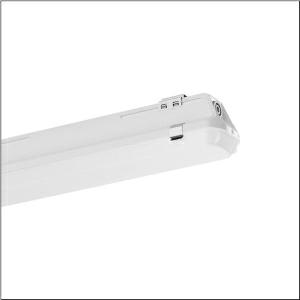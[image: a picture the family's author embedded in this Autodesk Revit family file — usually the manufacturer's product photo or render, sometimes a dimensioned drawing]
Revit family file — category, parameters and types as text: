
# Revit family: monsun_11_51fp10mp480h
name_source: partatom
category: Lighting Fixtures
units: mm (PartAtom-declared; Revit-internal decimal feet)

## family parameters
Cut with Voids When Loaded = No
Host = Face
Light Source = No
Part Type = Normal
Room Calculation Point = No
Round Connector Dimension = Use Diameter
Shared = No

## types (1)
- --- (1 x LED, 8070 lm, 45.4 W, 4000K)
    Apparent Load = 45 VA
    CIE Flux Codes = 47 77 93 94 100
    Color Rendering = 80
    Color Temperature = 4000K
    Default Elevation = 1800 mm
    Description = Monsun 11, damp-proof luminaire, chain hanger, primary optical cover: enclosure, of PMMA, light emission: direct distribution, primary light characteristic: symmetric, installation type: suspended mounting, surface-mounted, horizontal mounting, vertical mounting, LED, rated luminous flux: 8.070lm, luminous efficacy: 178lm/W, light colour: 840, colour temperature: 4000K, control gear: ON/OFF Multilumen, with terminal, 3-pole, max. 2.5mm², mains connection: 220..240V, AC, 50/60Hz, rated input power: 45W, luminaire housing, of glass-fibre reinforced polyester, uncoated, bright grey, incl. chain hanger, length: 1.590mm, width: 90mm, height: 88mm, clip for enclosure, of stainless steel (V2A), ceiling mounting element, of stainless steel (V2A), chain hanger, of stainless steel (V2A), protection rating (complete): IP66, insulation class (complete): insulation class I (protective earthing), certification: CE, ENEC, VDE, UKCA, protection symbol: D, impact resistance: IK04, permissible operating ambient temperature: -35..+40°C, standard: EN 50419, EN 60598-2-1, no direct snow, no direct sun, no direct rain, for indoor or canopied outdoor use, corresponds to IFS (International Featured Standards) requirements for safety and quality in the food industry, contact your sales advisor before using the luminaires in applications with unclear chemical exposure, large temperature fluctuations or condensation-forming humidity, LABS conformity tested according to VDMA 24364:2018-05, packaging unit: 1 piece
    Height = 89 mm
    Lamp = 1 x LED
    Lamp Light Flux = 8070 lm
    Lamp Power = 45.4 W
    Lamp count = 1
    Length = 1590 mm
    Luminous efficacy = 178 lm/W
    Manufacturer = Siteco
    ModVariant = No
    Model = 51FP10MP480H
    Mounting Place = Ceiling
    Mounting Type = Surface mounted
    Number of Poles = 1
    OnlyDefault = Yes
    Power Factor = 1
    Product Name = Monsun 11
    Product group = damp-proof luminaire
    ProductGroupID = 300
    Protection Class = Protection class I
    Protection Degree = IP 66
    RLX_Detail_Level = 1
    RLX_Emergency_Light_Flux = 0 lm
    RLX_Emergency_Type = 0
    RLX_Emergency_Type_DB = No
    RlxData = <blob elided: 90145 chars, md5=28a8cc23>
    Socket = socket
    Standby Power = 0 W
    System Light Flux = 8070 lm
    System Power = 45 W
    Type Comments = factory setting: luminous flux: 100 % | (A | C | E) | 105 mA
    Type Image = l_1349237.jpg
    URL = http://relux.com
    VarID = @adj_197499
    Voltage = 0 V
    Weight = 0.00 kg
    Width = 90 mm

## geometry (parser evidence)
native form markers: Blend x4, Sweep x13
no freeform markers — native parametric forms only
